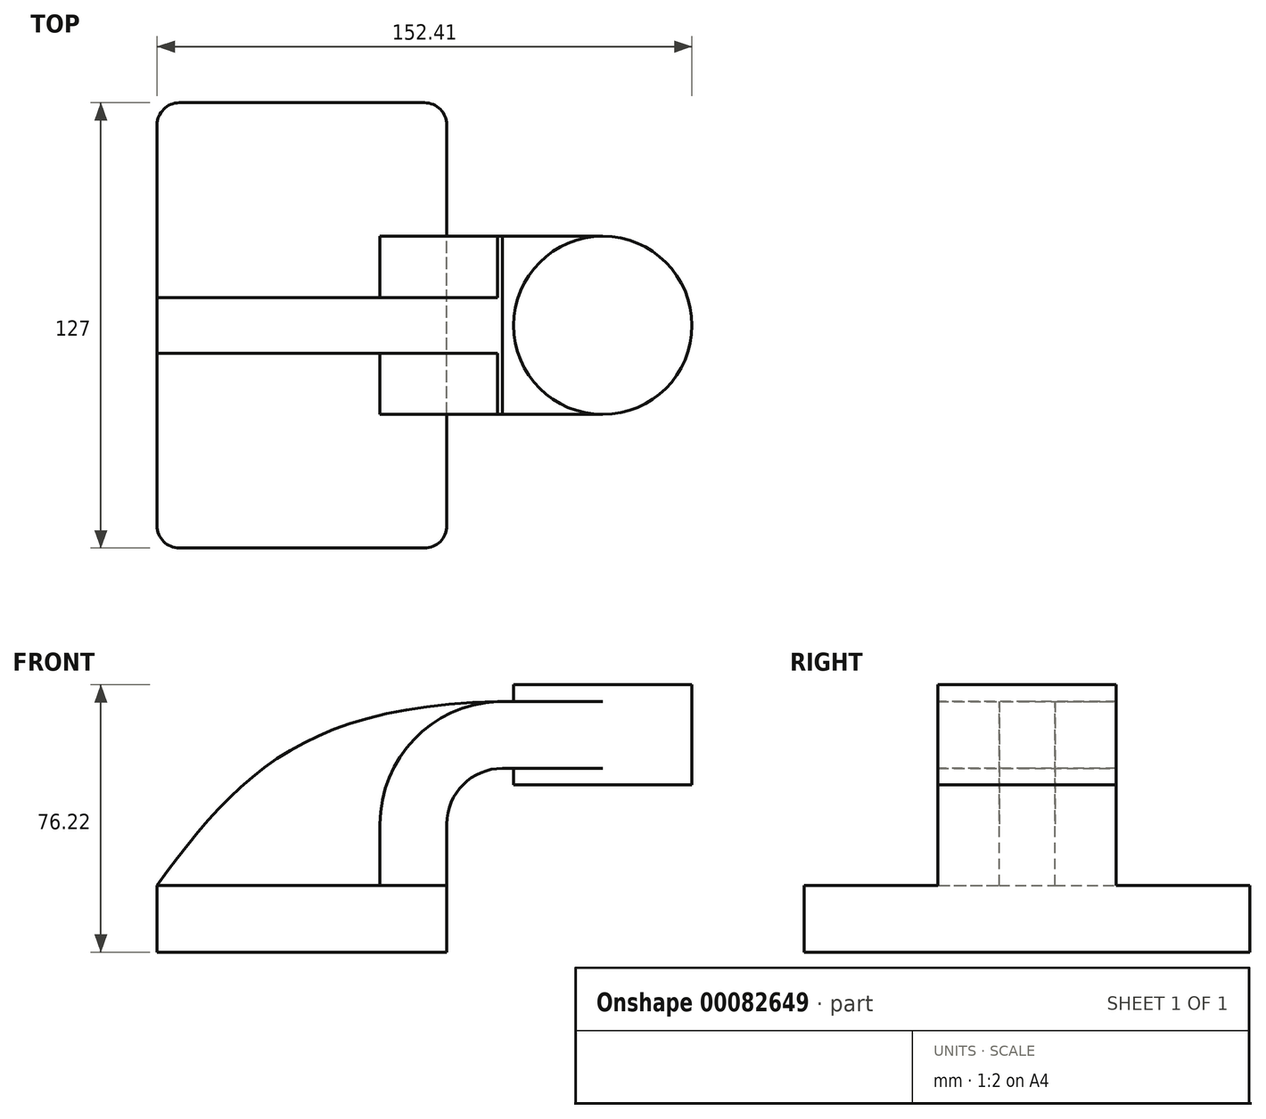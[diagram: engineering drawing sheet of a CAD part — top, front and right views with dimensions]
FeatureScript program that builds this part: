
annotation { "Feature Type Name" : "Feature", "Feature Type Description" : "" }
export const myFeature = defineFeature(function(context is Context, id is Id, definition is map)
    precondition{}
    {
        {
            var Q0;
            Q0=qCreatedBy(makeId("Front.planeOp"),FACE);
            var sketch = newSketch(context, id + "F0", { "sketchPlane" : qUnion([Q0])});
            skLineSegment(sketch, "E0.bottom", {"start": v(41.27, 9.53) * mm, "end": v(-41.28, 9.53) * mm});
            skLineSegment(sketch, "E0.top", {"start": v(41.28, -9.52) * mm, "end": v(-41.27, -9.52) * mm});
            skLineSegment(sketch, "E0.left", {"start": v(41.27, 9.53) * mm, "end": v(41.28, -9.52) * mm});
            skLineSegment(sketch, "E0.right", {"start": v(-41.28, 9.53) * mm, "end": v(-41.27, -9.52) * mm});
            skPoint(sketch, "E0.middle", {"position": v(0, 0) * mm});
            skLineSegment(sketch, "E1.bottom", {"start": v(60.32, 38.11) * mm, "end": v(111.12, 38.11) * mm});
            skLineSegment(sketch, "E1.top", {"start": v(60.32, 66.69) * mm, "end": v(111.12, 66.69) * mm});
            skLineSegment(sketch, "E1.left", {"start": v(60.32, 38.11) * mm, "end": v(60.32, 66.69) * mm});
            skLineSegment(sketch, "E1.right", {"start": v(111.12, 38.11) * mm, "end": v(111.12, 66.69) * mm});
            skPoint(sketch, "E1.middle", {"position": v(85.72, 52.4) * mm});
            skLineSegment(sketch, "E2", {"start": v(41.27, 9.53) * mm, "end": v(41.27, 27) * mm});
            skArc(sketch, "E3", {"start": v(41.27, 27) * mm, "mid": v(45.92, 38.23) * mm, "end": v(57.15, 42.88) * mm});
            skLineSegment(sketch, "E4", {"start": v(57.15, 42.88) * mm, "end": v(85.72, 42.88) * mm});
            skLineSegment(sketch, "E5.0", {"start": v(57.15, 61.93) * mm, "end": v(85.72, 61.93) * mm});
            skArc(sketch, "E5.1", {"start": v(22.22, 27) * mm, "mid": v(32.45, 51.7) * mm, "end": v(57.15, 61.93) * mm});
            skLineSegment(sketch, "E5.2", {"start": v(22.22, 9.53) * mm, "end": v(22.22, 27) * mm});
            skFitSpline(sketch, "E6", {"points": [v(-41.28, 9.53) * mm, v(57.15, 61.93) * mm], "startDerivative": vector(68.68, 93.7) * mm, "endDerivative": vector(171.45, 3.11) * mm});
            skLineSegment(sketch, "E7", {"start": v(85.72, 38.11) * mm, "end": v(85.72, 66.69) * mm});
            skSolve(sketch);
        }
        {
            var Q0;
            Q0=makeQuery(id+"F0.imprint","IMPRINT",FACE,{"disambiguationData":[TD([[makeQuery(id+"F0.imprint","IMPRINT",EDGE,{"derivedFrom":sQuery(id+"F0.wireOp",EDGE,"E0.top")}),-1.0]])]});
            extrude(context, id + "F1", {"entities" : qUnion([Q0]), "endBound" : BoundingType.SYMMETRIC, "depth" : 127 * mm});
        }
        {
            var Q0;
            {var subQ1=sQuery(id+"F0.wireOp",EDGE,"E2");Q0=makeQuery(id+"F0.imprint","IMPRINT",FACE,{"disambiguationData":[TD([[makeQuery(id+"F0.imprint","IMPRINT",EDGE,{"derivedFrom":subQ1}),1.0]])]});}
            var Q1;
            {var subQ0=sQuery(id+"F0.wireOp",EDGE,"E4");var subQ1=sQuery(id+"F0.wireOp",EDGE,"E1.left");var subQ2=makeQuery(id+"F0.imprint","INTERSECT",VERTEX,{"derivedFrom":[subQ1,subQ0]});Q1=makeQuery(id+"F0.imprint","IMPRINT",FACE,{"disambiguationData":[TD([[makeQuery(id+"F0.imprint","IMPRINT",EDGE,{"disambiguationData":[TD([[subQ2,-1.0]])],"derivedFrom":subQ1}),-1.0]])]});}
            extrude(context, id + "F2", {"entities" : qUnion([Q0, Q1]), "operationType" : NewBodyOperationType.ADD, "endBound" : BoundingType.SYMMETRIC, "depth" : 50.8 * mm});
        }
        {
            var Q0;
            {var subQ3=sQuery(id+"F0.wireOp",EDGE,"E5.2");Q0=makeQuery(id+"F0.imprint","IMPRINT",FACE,{"disambiguationData":[TD([[makeQuery(id+"F0.imprint","IMPRINT",EDGE,{"derivedFrom":subQ3}),1.0]])]});}
            extrude(context, id + "F3", {"entities" : qUnion([Q0]), "operationType" : NewBodyOperationType.ADD, "endBound" : BoundingType.SYMMETRIC, "depth" : 15.88 * mm});
        }
        {
            var Q0;
            {var subQ0=sQuery(id+"F0.wireOp",EDGE,"E1.right");Q0=makeQuery(id+"F0.imprint","IMPRINT",FACE,{"disambiguationData":[TD([[makeQuery(id+"F0.imprint","IMPRINT",EDGE,{"derivedFrom":subQ0}),1.0]])]});}
            var Q1;
            Q1=sQuery(id+"F0.wireOp",EDGE,"E7");
            revolve(context, id + "F4", {"operationType" : NewBodyOperationType.ADD, "entities" : qUnion([Q0]), "axis" : qUnion([Q1]), "revolveType" : RevolveType.FULL});
        }
        {
            var Q0;
            Q0=makeQuery(id+"F1.opExtrude","CAP_EDGE",EDGE,{"disambiguationData":[OSD([sQuery(id+"F0.wireOp",EDGE,"E0.left")])],"isStart":false});
            var Q1;
            Q1=makeQuery(id+"F1.opExtrude","CAP_EDGE",EDGE,{"disambiguationData":[OSD([sQuery(id+"F0.wireOp",EDGE,"E0.right")])],"isStart":false});
            var Q2;
            Q2=makeQuery(id+"F1.opExtrude","CAP_EDGE",EDGE,{"disambiguationData":[OSD([sQuery(id+"F0.wireOp",EDGE,"E0.left")])],"isStart":true});
            var Q3;
            Q3=makeQuery(id+"F1.opExtrude","CAP_EDGE",EDGE,{"disambiguationData":[OSD([sQuery(id+"F0.wireOp",EDGE,"E0.right")])],"isStart":true});
            fillet(context, id + "F5", {"entities" : qUnion([Q0, Q1, Q2, Q3]), "radius" : 6.35 * mm, "tangentPropagation" : true, "allowEdgeOverflow" : false});
        }
    });
